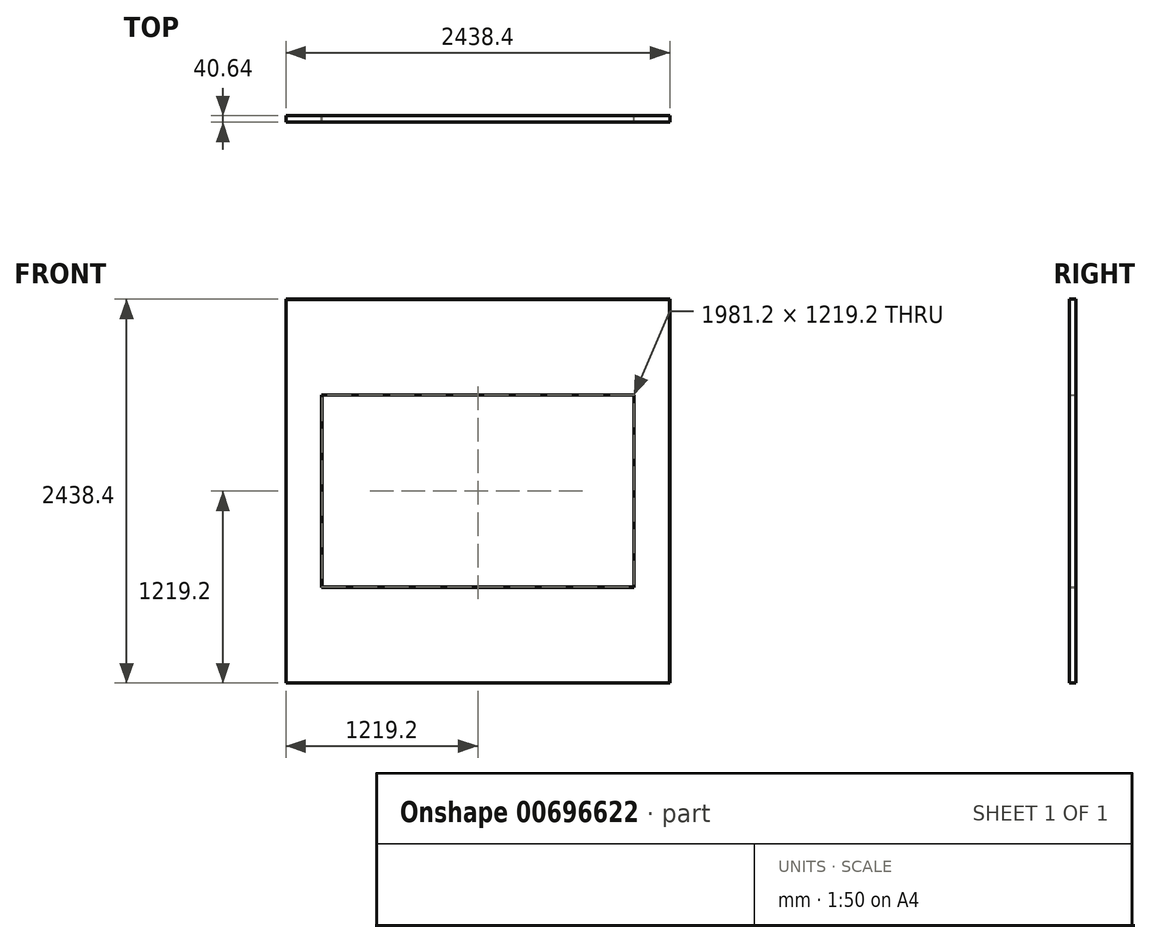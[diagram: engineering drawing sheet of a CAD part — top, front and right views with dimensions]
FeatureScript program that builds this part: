
annotation { "Feature Type Name" : "Feature", "Feature Type Description" : "" }
export const myFeature = defineFeature(function(context is Context, id is Id, definition is map)
    precondition{}
    {
        {
            var Q0;
            Q0=qCreatedBy(makeId("Front.planeOp"),FACE);
            var sketch = newSketch(context, id + "F0", { "sketchPlane" : qUnion([Q0])});
            skLineSegment(sketch, "E0.bottom", {"start": v(-1219.2, 1219.2) * mm, "end": v(1219.2, 1219.2) * mm});
            skLineSegment(sketch, "E0.top", {"start": v(-1219.2, -1219.2) * mm, "end": v(1219.2, -1219.2) * mm});
            skLineSegment(sketch, "E0.left", {"start": v(-1219.2, 1219.2) * mm, "end": v(-1219.2, -1219.2) * mm});
            skLineSegment(sketch, "E0.right", {"start": v(1219.2, 1219.2) * mm, "end": v(1219.2, -1219.2) * mm});
            skPoint(sketch, "E0.middle", {"position": v(0, 0) * mm});
            skLineSegment(sketch, "E1.bottom", {"start": v(990.6, 609.6) * mm, "end": v(-990.6, 609.6) * mm});
            skLineSegment(sketch, "E1.top", {"start": v(990.6, -609.6) * mm, "end": v(-990.6, -609.6) * mm});
            skLineSegment(sketch, "E1.left", {"start": v(990.6, 609.6) * mm, "end": v(990.6, -609.6) * mm});
            skLineSegment(sketch, "E1.right", {"start": v(-990.6, 609.6) * mm, "end": v(-990.6, -609.6) * mm});
            skSolve(sketch);
        }
        {
            var Q0;
            Q0=makeQuery(id+"F0.imprint","IMPRINT",FACE,{"disambiguationData":[TD([[makeQuery(id+"F0.imprint","IMPRINT",EDGE,{"derivedFrom":sQuery(id+"F0.wireOp",EDGE,"E0.bottom")}),-1.0]])]});
            extrude(context, id + "F1", {"entities" : qUnion([Q0]), "depth" : 40.64 * mm, "offsetDistance" : 25.4 * mm});
        }
        {
            var Q0;
            Q0=makeQuery(id+"F1.opExtrude","CAP_FACE",FACE,{"disambiguationData":[OSD([sQuery(id+"F0.wireOp",EDGE,"E0.bottom"),sQuery(id+"F0.wireOp",EDGE,"E0.top"),sQuery(id+"F0.wireOp",EDGE,"E0.left"),sQuery(id+"F0.wireOp",EDGE,"E0.right"),sQuery(id+"F0.wireOp",EDGE,"E1.bottom"),sQuery(id+"F0.wireOp",EDGE,"E1.top"),sQuery(id+"F0.wireOp",EDGE,"E1.left"),sQuery(id+"F0.wireOp",EDGE,"E1.right")])],"isStart":false});
            shell(context, id + "F2", {"entities" : qUnion([Q0]), "thickness" : 2.54 * mm});
        }
    });
